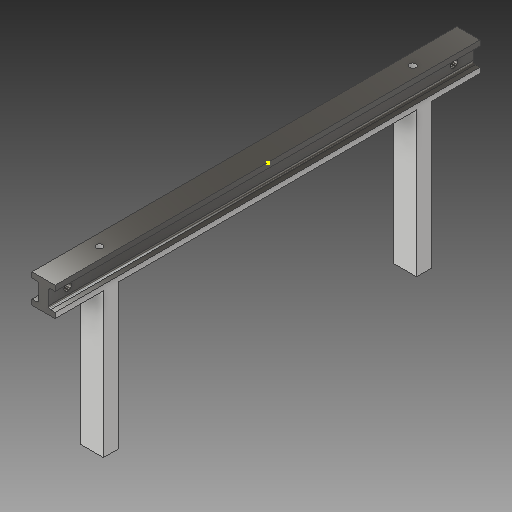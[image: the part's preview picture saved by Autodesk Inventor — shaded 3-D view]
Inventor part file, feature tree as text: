
AUTODESK INVENTOR PART (.ipt)
format: ipt  version: 2019 (Build 230136000, 136)  size: 194,048 bytes
history: native  units: mm
features: sketch x6, hole x4, extrude x2
ambient origin geometry x8: Origin, YZ Plane, XZ Plane, XY Plane, X Axis, Y Axis, Z Axis, Center Point
bodies: Solid1 (feature_tree)
feature tree (12):
  extrude  "Extrusion1"  Depth=38.0mm
  hole  "Hole1"  [1 undecoded]
  hole  "Hole2"  [1 undecoded]
  extrude  "Extrusion2"  Depth=7.0mm
  sketch  "Sketch5"  dims[d4=9.0mm d6=7.0mm]
  hole  "Hole6"  [1 undecoded]
  hole  "Hole7"  [1 undecoded]
  sketch  "Sketch1"  dims[d0=30.5mm d1=38.0mm]
  sketch  "Sketch2"  dims[d2=7.0mm d3=7.0mm]
  sketch  "Sketch7"  dims[d7=9.0mm d8=7.0mm]
  sketch  "Sketch10"  dims[d9=3.0mm d11=3.0mm]
  sketch  "Sketch11"  dims[d12=558.8mm d13=0.0mm d14=25.4mm d24=9.0mm d16=10.0mm d17=6.0mm d18=4.0mm d19=2.0mm d20=90.0deg d21=25.0mm d22=0.0mm d23=25.4mm d25=9.0mm d26=10.0mm d27=6.0mm d28=4.0mm d29=2.0mm d30=90.0deg d31=25.0mm d32=20.594885mm d33=63.5mm d34=20.0mm d35=30.5mm d36=63.5mm d37=20.0mm d38=190.0mm d39=0.0mm d82=15.0mm d83=10.0mm d84=8.647mm d85=20.0mm d86=4.0mm d87=2.0mm d88=90.0deg d89=8.0mm d90=20.594885mm d91=15.0mm d92=10.0mm d93=8.647mm d94=20.0mm d95=4.0mm d96=2.0mm d97=90.0deg d98=8.0mm d99=20.594885mm]
note: 4 required parameter values undecoded (feature->parameter linkage not recoverable at this tier; creation-order binding heuristic only, values carry confidence <= 0.55)
